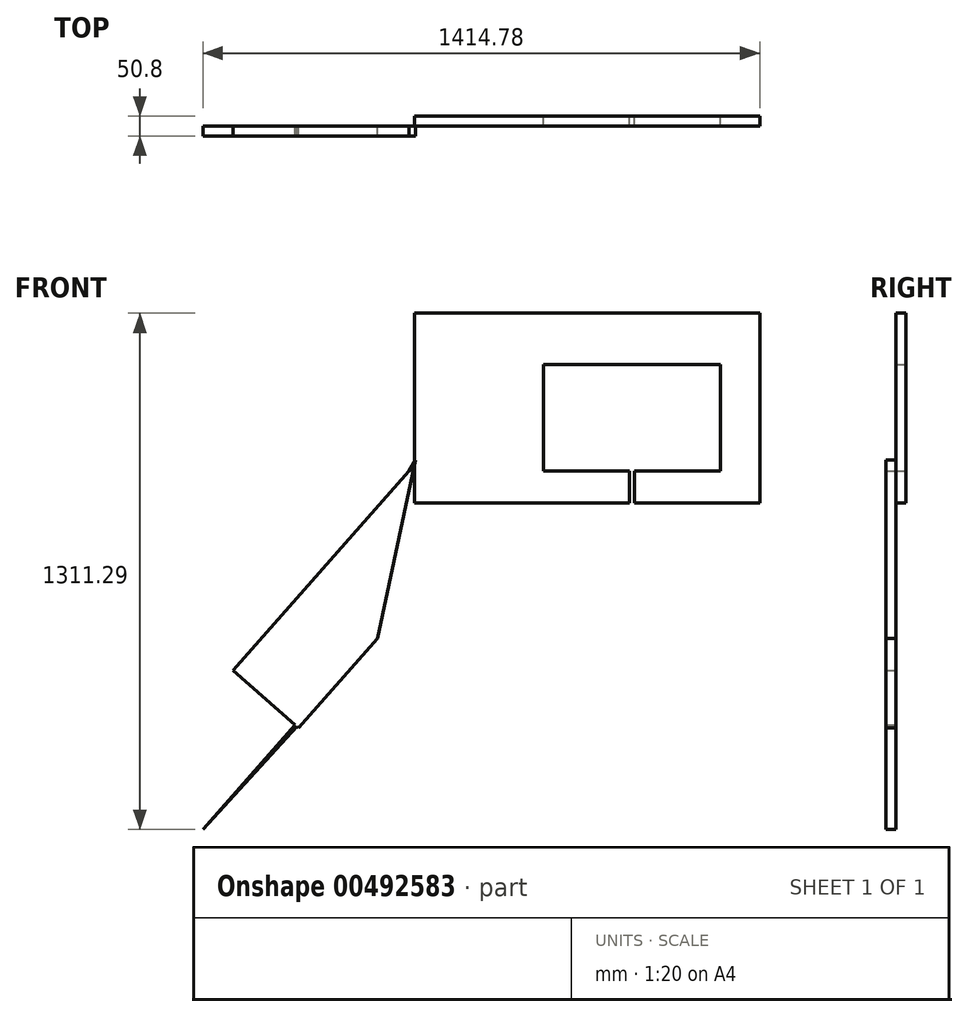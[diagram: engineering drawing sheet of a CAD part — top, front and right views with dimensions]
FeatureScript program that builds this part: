
annotation { "Feature Type Name" : "Feature", "Feature Type Description" : "" }
export const myFeature = defineFeature(function(context is Context, id is Id, definition is map)
    precondition{}
    {
        {
            var Q0;
            Q0=qCreatedBy(makeId("Front.planeOp"),FACE);
            var sketch = newSketch(context, id + "F0", { "sketchPlane" : qUnion([Q0])});
            skLineSegment(sketch, "E0.bottom", {"start": v(-225.13, 271.06) * mm, "end": v(225.13, 271.06) * mm});
            skLineSegment(sketch, "E0.top", {"start": v(-225.13, 0) * mm, "end": v(225.13, 0) * mm});
            skLineSegment(sketch, "E0.left", {"start": v(-225.13, 271.06) * mm, "end": v(-225.13, 0) * mm});
            skLineSegment(sketch, "E0.right", {"start": v(225.13, 271.06) * mm, "end": v(225.13, 0) * mm});
            skPoint(sketch, "E0.middle", {"position": v(0, 135.52) * mm});
            skLineSegment(sketch, "E1.bottom", {"start": v(-6.51, 0) * mm, "end": v(6.51, 0) * mm});
            skLineSegment(sketch, "E1.top", {"start": v(-6.51, -272.15) * mm, "end": v(6.51, -272.15) * mm});
            skLineSegment(sketch, "E1.left", {"start": v(-6.51, 0) * mm, "end": v(-6.51, -272.15) * mm});
            skLineSegment(sketch, "E1.right", {"start": v(6.51, 0) * mm, "end": v(6.51, -272.15) * mm});
            skPoint(sketch, "E1.middle", {"position": v(0, -136.08) * mm});
            skLineSegment(sketch, "E2.bottom", {"start": v(324.49, -81.08) * mm, "end": v(-552.23, -81.08) * mm});
            skLineSegment(sketch, "E2.top", {"start": v(324.49, 400.95) * mm, "end": v(-552.23, 400.95) * mm});
            skLineSegment(sketch, "E2.left", {"start": v(324.49, -81.08) * mm, "end": v(324.49, 400.95) * mm});
            skLineSegment(sketch, "E2.right", {"start": v(-552.23, -81.08) * mm, "end": v(-552.23, 400.95) * mm});
            skPoint(sketch, "E2.middle", {"position": v(-113.87, 159.94) * mm});
            skSolve(sketch);
        }
        {
            var Q0;
            Q0=makeQuery(id+"F0.imprint","IMPRINT",FACE,{"disambiguationData":[TD([[makeQuery(id+"F0.imprint","IMPRINT",EDGE,{"derivedFrom":sQuery(id+"F0.wireOp",EDGE,"E0.bottom")}),1.0]])]});
            extrude(context, id + "F1", {"entities" : qUnion([Q0]), "depth" : 25.4 * mm});
        }
        {
            var Q0;
            Q0=makeQuery(id+"F1.opExtrude","CAP_FACE",FACE,{"disambiguationData":[OSD([sQuery(id+"F0.wireOp",EDGE,"E0.bottom"),sQuery(id+"F0.wireOp",EDGE,"E0.top"),sQuery(id+"F0.wireOp",EDGE,"E0.left"),sQuery(id+"F0.wireOp",EDGE,"E0.right"),sQuery(id+"F0.wireOp",EDGE,"E1.left"),sQuery(id+"F0.wireOp",EDGE,"E1.right"),sQuery(id+"F0.wireOp",EDGE,"E2.bottom"),sQuery(id+"F0.wireOp",EDGE,"E2.top"),sQuery(id+"F0.wireOp",EDGE,"E2.left"),sQuery(id+"F0.wireOp",EDGE,"E2.right")])],"isStart":false});
            var sketch = newSketch(context, id + "F2", { "sketchPlane" : qUnion([Q0])});
            skLineSegment(sketch, "E3", {"start": v(-271.05, 0) * mm, "end": v(-847.65, -652.83) * mm});
            skLineSegment(sketch, "E4", {"start": v(-847.65, -652.83) * mm, "end": v(-1013.38, -506.45) * mm});
            skLineSegment(sketch, "E5", {"start": v(-1013.38, -506.45) * mm, "end": v(-566.07, 0) * mm});
            skLineSegment(sketch, "E6", {"start": v(-566.07, 0) * mm, "end": v(-550.17, 27.64) * mm});
            skLineSegment(sketch, "E7", {"start": v(-550.17, 27.64) * mm, "end": v(-646.67, -425.28) * mm});
            skLineSegment(sketch, "E8", {"start": v(-646.67, -425.28) * mm, "end": v(-1090.29, -910.34) * mm});
            skLineSegment(sketch, "E9", {"start": v(-1090.29, -910.34) * mm, "end": v(-748.6, -522.78) * mm});
            skSolve(sketch);
        }
        {
            var Q0;
            Q0 = qSketchRegion(id + "F2", true);
            var Q1;
            {var subQ1=sQuery(id+"F2.wireOp",EDGE,"E5");Q1=makeQuery(id+"F2.imprint","IMPRINT",FACE,{"disambiguationData":[TD([[makeQuery(id+"F2.imprint","IMPRINT",EDGE,{"derivedFrom":subQ1}),-1.0]])]});}
            extrude(context, id + "F3", {"entities" : qUnion([Q0, Q1]), "operationType" : NewBodyOperationType.ADD, "depth" : 25.4 * mm, "offsetDistance" : 25.4 * mm});
        }
    });
